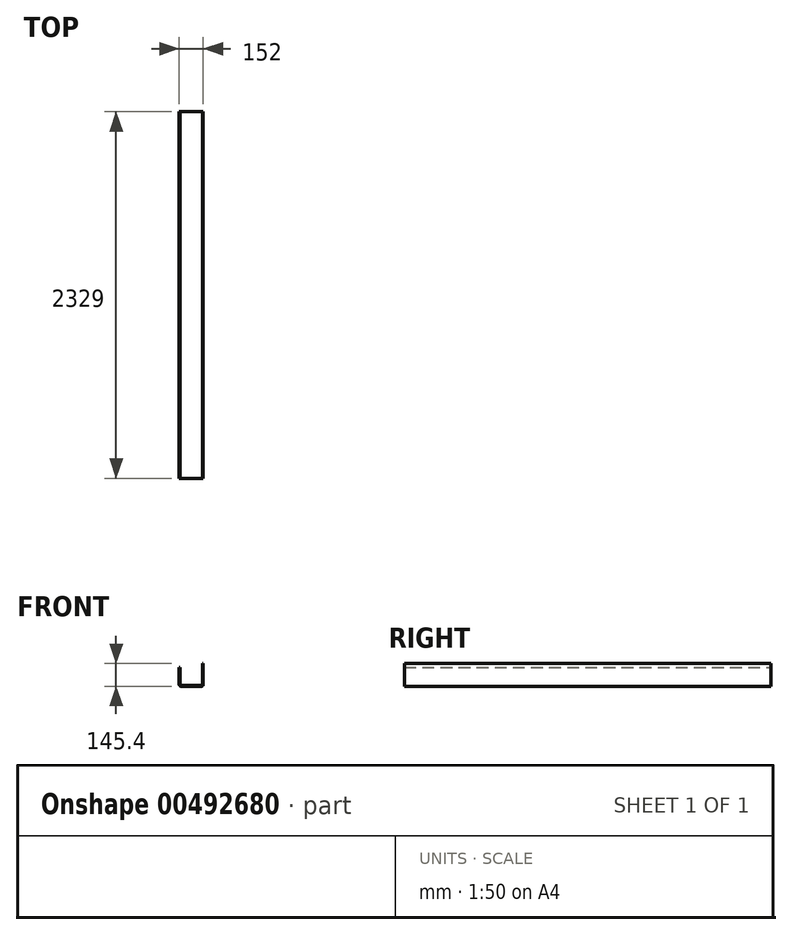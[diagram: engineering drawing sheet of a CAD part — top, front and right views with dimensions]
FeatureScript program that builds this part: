
annotation { "Feature Type Name" : "Feature", "Feature Type Description" : "" }
export const myFeature = defineFeature(function(context is Context, id is Id, definition is map)
    precondition{}
    {
        {
            var Q0;
            Q0=qCreatedBy(makeId("Front.planeOp"),FACE);
            var sketch = newSketch(context, id + "F0", { "sketchPlane" : qUnion([Q0])});
            skLineSegment(sketch, "E0", {"start": v(10, 0) * mm, "end": v(142, 0) * mm});
            skLineSegment(sketch, "E1", {"start": v(0, 10) * mm, "end": v(0, 120) * mm});
            skLineSegment(sketch, "E2", {"start": v(152, 10) * mm, "end": v(152, 145.4) * mm});
            skLineSegment(sketch, "E3.0", {"start": v(4.5, 14.5) * mm, "end": v(4.5, 120) * mm});
            skLineSegment(sketch, "E3.1", {"start": v(14.5, 4.5) * mm, "end": v(137.5, 4.5) * mm});
            skLineSegment(sketch, "E3.2", {"start": v(147.5, 14.5) * mm, "end": v(147.5, 145.4) * mm});
            skLineSegment(sketch, "E4", {"start": v(0, 120) * mm, "end": v(4.5, 120) * mm});
            skLineSegment(sketch, "E5", {"start": v(147.5, 145.4) * mm, "end": v(152, 145.4) * mm});
            skPoint(sketch, "E6.visualSharp", {"position": v(152, 0) * mm});
            skArc(sketch, "E6.filletArc", {"start": v(142, 0) * mm, "mid": v(149.07, 2.93) * mm, "end": v(152, 10) * mm});
            skPoint(sketch, "E7.visualSharp", {"position": v(147.5, 4.5) * mm});
            skArc(sketch, "E7.filletArc", {"start": v(137.5, 4.5) * mm, "mid": v(144.57, 7.43) * mm, "end": v(147.5, 14.5) * mm});
            skPoint(sketch, "E8.visualSharp", {"position": v(0, 0) * mm});
            skArc(sketch, "E8.filletArc", {"start": v(0, 10) * mm, "mid": v(2.93, 2.93) * mm, "end": v(10, 0) * mm});
            skPoint(sketch, "E9.visualSharp", {"position": v(4.5, 4.5) * mm});
            skArc(sketch, "E9.filletArc", {"start": v(4.5, 14.5) * mm, "mid": v(7.43, 7.43) * mm, "end": v(14.5, 4.5) * mm});
            skSolve(sketch);
        }
        {
            var Q0;
            Q0=makeQuery(id+"F0.imprint","IMPRINT",FACE,{"disambiguationData":[TD([[makeQuery(id+"F0.imprint","IMPRINT",EDGE,{"derivedFrom":sQuery(id+"F0.wireOp",EDGE,"E0")}),1.0]])]});
            extrude(context, id + "F1", {"entities" : qUnion([Q0]), "depth" : 2329 * mm});
        }
    });
